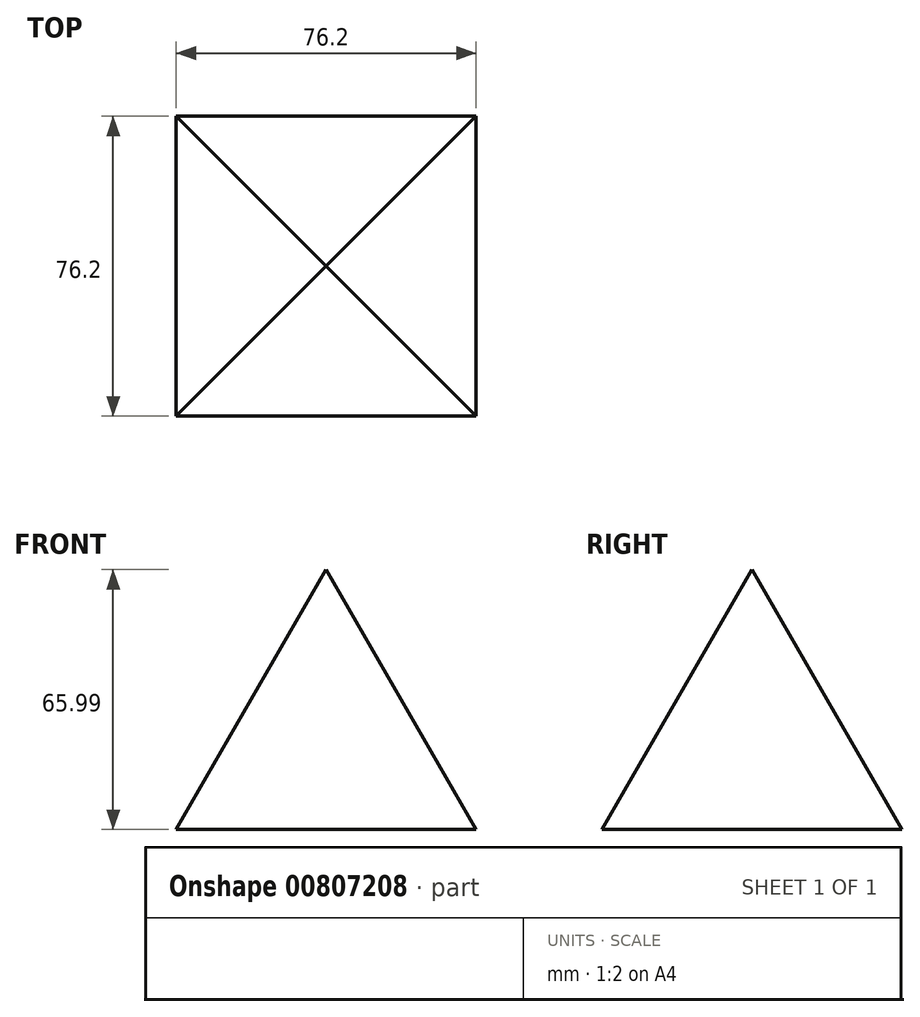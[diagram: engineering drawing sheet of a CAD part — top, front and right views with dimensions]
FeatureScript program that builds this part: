
annotation { "Feature Type Name" : "Feature", "Feature Type Description" : "" }
export const myFeature = defineFeature(function(context is Context, id is Id, definition is map)
    precondition{}
    {
        {
            var Q0;
            Q0=qCreatedBy(makeId("Top.planeOp"),FACE);
            var sketch = newSketch(context, id + "F0", { "sketchPlane" : qUnion([Q0])});
            skLineSegment(sketch, "E0.bottom", {"start": v(-158.96, -205.74) * mm, "end": v(-202.64, -205.74) * mm});
            skLineSegment(sketch, "E0.top", {"start": v(-158.96, -210.8) * mm, "end": v(-202.64, -210.8) * mm});
            skLineSegment(sketch, "E0.left", {"start": v(-158.96, -205.74) * mm, "end": v(-158.96, -210.8) * mm});
            skLineSegment(sketch, "E0.right", {"start": v(-202.64, -205.74) * mm, "end": v(-202.64, -210.8) * mm});
            skLineSegment(sketch, "E1.bottom", {"start": v(-166.52, -210.8) * mm, "end": v(-172.28, -210.8) * mm});
            skLineSegment(sketch, "E1.top", {"start": v(-166.52, -205.74) * mm, "end": v(-172.28, -205.74) * mm});
            skLineSegment(sketch, "E1.left", {"start": v(-166.52, -210.8) * mm, "end": v(-166.52, -205.74) * mm});
            skLineSegment(sketch, "E1.right", {"start": v(-172.28, -210.8) * mm, "end": v(-172.28, -205.74) * mm});
            skLineSegment(sketch, "E2.bottom", {"start": v(-27.78, 24.23) * mm, "end": v(48.42, 24.23) * mm});
            skLineSegment(sketch, "E2.top", {"start": v(-27.78, -51.97) * mm, "end": v(48.42, -51.97) * mm});
            skLineSegment(sketch, "E2.left", {"start": v(-27.78, 24.23) * mm, "end": v(-27.78, -51.97) * mm});
            skLineSegment(sketch, "E2.right", {"start": v(48.42, 24.23) * mm, "end": v(48.42, -51.97) * mm});
            skSolve(sketch);
        }
        {
            var Q0;
            Q0=makeQuery(id+"F0.imprint","IMPRINT",FACE,{"disambiguationData":[TD([[makeQuery(id+"F0.imprint","IMPRINT",EDGE,{"derivedFrom":sQuery(id+"F0.wireOp",EDGE,"E2.bottom")}),-1.0]])]});
            extrude(context, id + "F1", {"entities" : qUnion([Q0]), "depth" : 112.52 * mm, "offsetDistance" : 25.4 * mm, "hasDraft" : true, "draftAngle" : 30 * degree, "draftPullDirection" : true});
        }
    });
